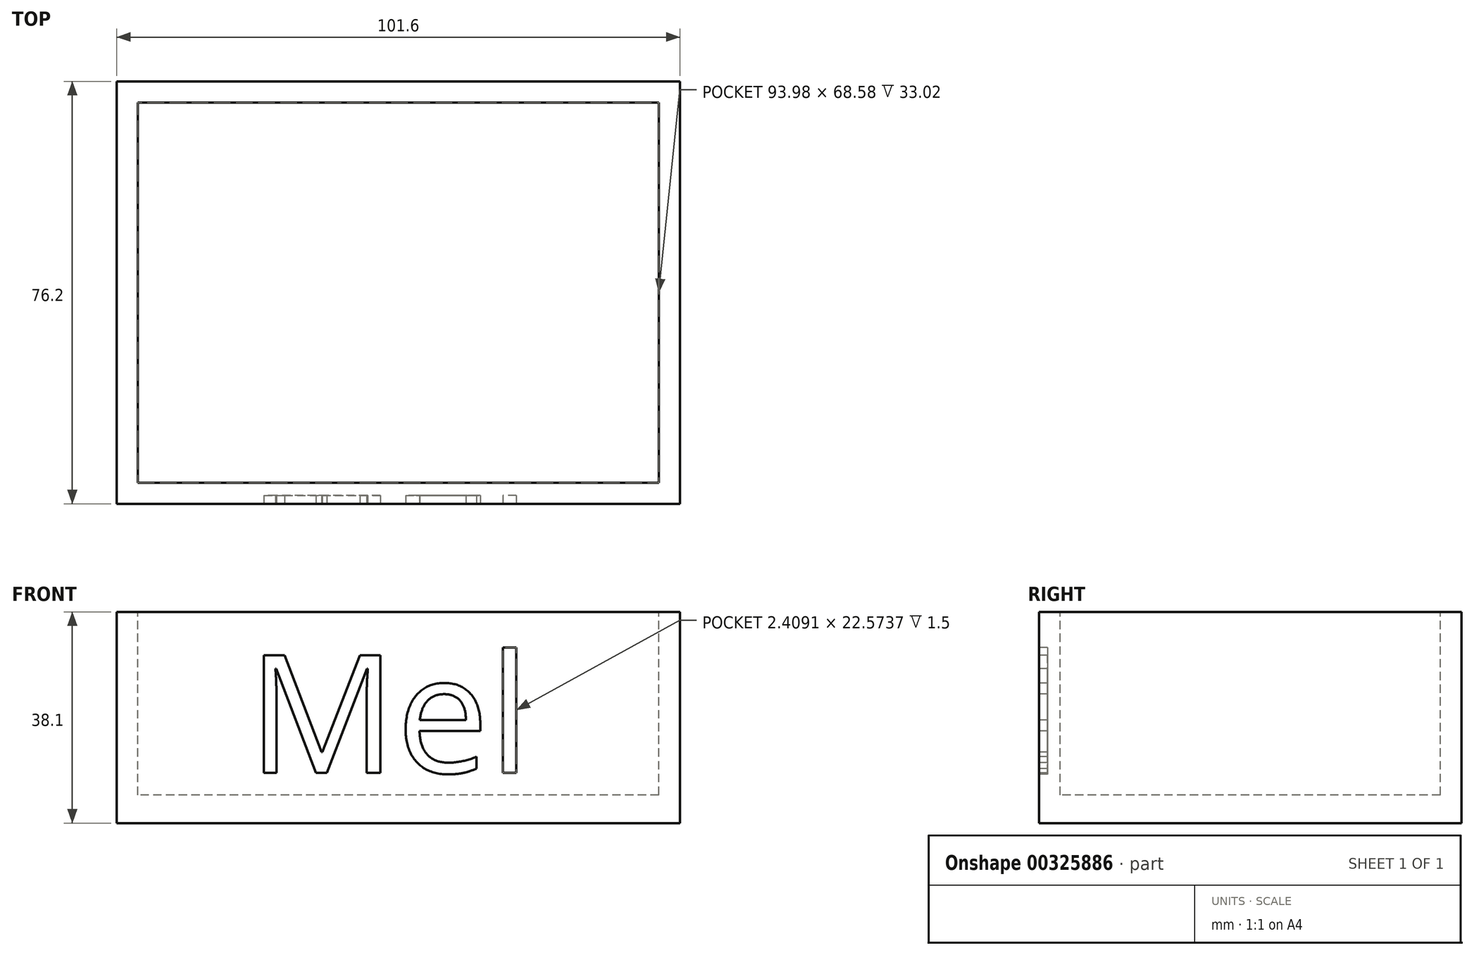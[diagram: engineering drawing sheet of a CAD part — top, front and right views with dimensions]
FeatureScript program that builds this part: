
annotation { "Feature Type Name" : "Feature", "Feature Type Description" : "" }
export const myFeature = defineFeature(function(context is Context, id is Id, definition is map)
    precondition{}
    {
        {
            var Q0;
            Q0=qCreatedBy(makeId("Top.planeOp"),FACE);
            var sketch = newSketch(context, id + "F0", { "sketchPlane" : qUnion([Q0])});
            skLineSegment(sketch, "E0.bottom", {"start": v(50.8, 38.1) * mm, "end": v(-50.8, 38.1) * mm});
            skLineSegment(sketch, "E0.top", {"start": v(50.8, -38.1) * mm, "end": v(-50.8, -38.1) * mm});
            skLineSegment(sketch, "E0.left", {"start": v(50.8, 38.1) * mm, "end": v(50.8, -38.1) * mm});
            skLineSegment(sketch, "E0.right", {"start": v(-50.8, 38.1) * mm, "end": v(-50.8, -38.1) * mm});
            skPoint(sketch, "E0.middle", {"position": v(0, 0) * mm});
            skSolve(sketch);
        }
        {
            var Q0;
            Q0=makeQuery(id+"F0.imprint","IMPRINT",FACE,{"disambiguationData":[TD([[makeQuery(id+"F0.imprint","IMPRINT",EDGE,{"derivedFrom":sQuery(id+"F0.wireOp",EDGE,"E0.bottom")}),1.0]])]});
            extrude(context, id + "F1", {"entities" : qUnion([Q0]), "depth" : 38.1 * mm});
        }
        {
            var Q0;
            Q0=makeQuery(id+"F1.opExtrude","CAP_FACE",FACE,{"disambiguationData":[OSD([sQuery(id+"F0.wireOp",EDGE,"E0.bottom"),sQuery(id+"F0.wireOp",EDGE,"E0.top"),sQuery(id+"F0.wireOp",EDGE,"E0.left"),sQuery(id+"F0.wireOp",EDGE,"E0.right")])],"isStart":false});
            var sketch = newSketch(context, id + "F2", { "sketchPlane" : qUnion([Q0])});
            skLineSegment(sketch, "E1.bottom", {"start": v(47, 34.3) * mm, "end": v(-47, 34.3) * mm});
            skLineSegment(sketch, "E1.top", {"start": v(47, -34.3) * mm, "end": v(-47, -34.3) * mm});
            skLineSegment(sketch, "E1.left", {"start": v(47, 34.3) * mm, "end": v(46.99, -34.3) * mm});
            skLineSegment(sketch, "E1.right", {"start": v(-46.99, 34.3) * mm, "end": v(-47, -34.3) * mm});
            skPoint(sketch, "E1.middle", {"position": v(0, 0) * mm});
            skSolve(sketch);
        }
        {
            var Q0;
            Q0 = qSketchRegion(id + "F2", true);
            extrude(context, id + "F3", {"entities" : qUnion([Q0]), "operationType" : NewBodyOperationType.REMOVE, "oppositeDirection" : true, "depth" : 33.02 * mm});
        }
        {
            var Q0;
            Q0=makeQuery(id+"F1.opExtrude","SWEPT_FACE",FACE,{"disambiguationData":[OSD([sQuery(id+"F0.wireOp",EDGE,"E0.top")])]});
            var sketch = newSketch(context, id + "F4", { "sketchPlane" : qUnion([Q0])});
            skText(sketch, "E2", { "text": "Mel", "fontName": "OpenSans-Regular.ttf"});
            const initialGuessF4  = {"E2": [-0.02717, 0.00908, 1, 0, 0.02139]};
            skSetInitialGuess(sketch, initialGuessF4);
            skSolve(sketch);
        }
        {
            var Q0;
            Q0 = qSketchRegion(id + "F4", true);
            extrude(context, id + "F5", {"entities" : qUnion([Q0]), "operationType" : NewBodyOperationType.REMOVE, "oppositeDirection" : true, "depth" : 1.5 * mm});
        }
    });
